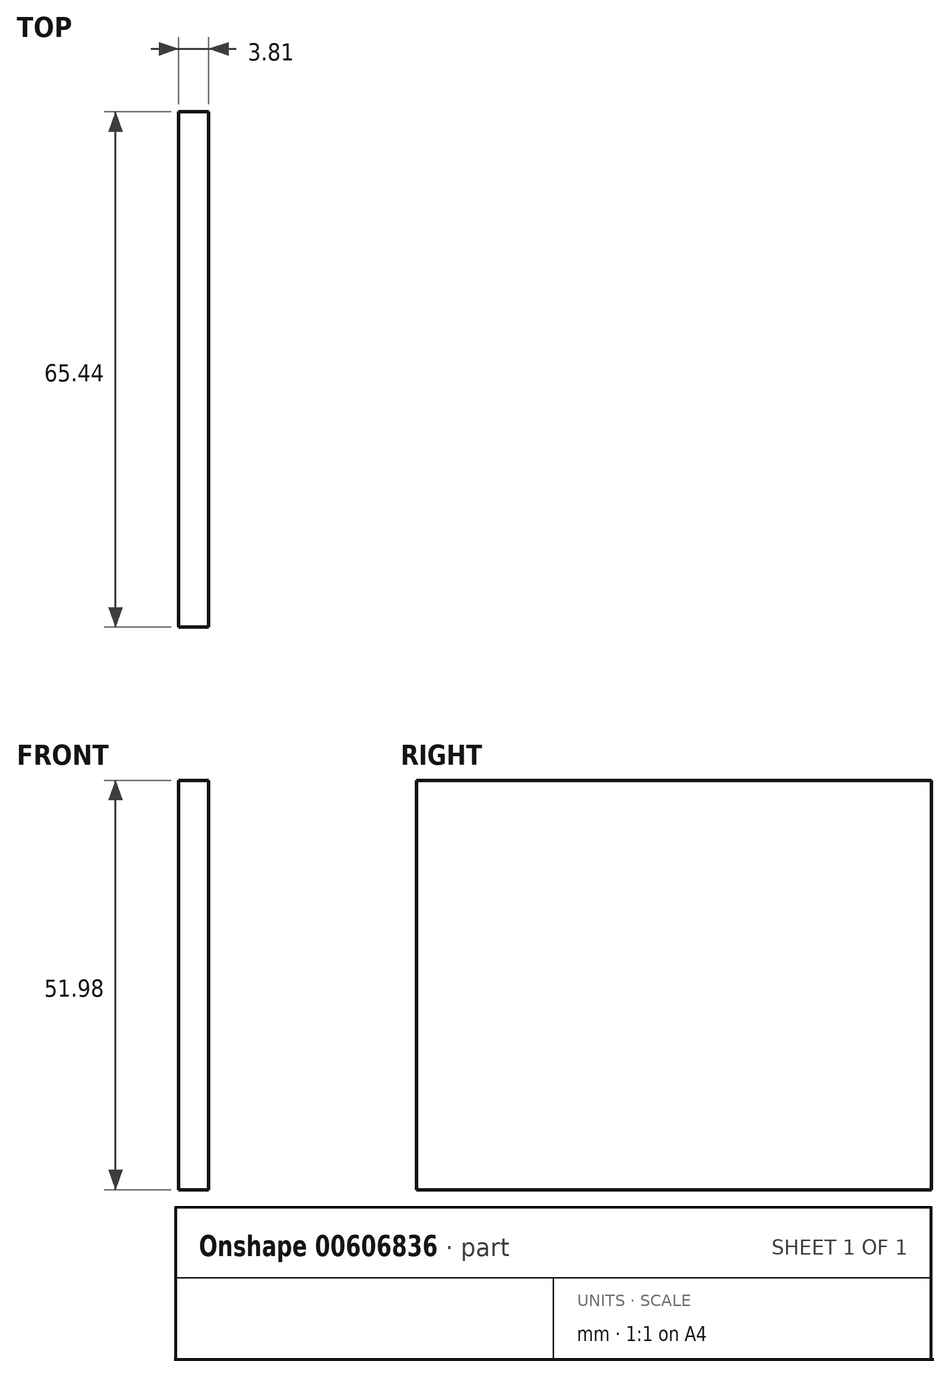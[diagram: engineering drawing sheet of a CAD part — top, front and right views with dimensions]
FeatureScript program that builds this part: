
annotation { "Feature Type Name" : "Feature", "Feature Type Description" : "" }
export const myFeature = defineFeature(function(context is Context, id is Id, definition is map)
    precondition{}
    {
        {
            var Q0;
            Q0=qCreatedBy(makeId("Right.planeOp"),FACE);
            var sketch = newSketch(context, id + "F0", { "sketchPlane" : qUnion([Q0])});
            skLineSegment(sketch, "E0.bottom", {"start": v(-65.44, 51.98) * mm, "end": v(0, 51.98) * mm});
            skLineSegment(sketch, "E0.top", {"start": v(-65.44, 0) * mm, "end": v(0, 0) * mm});
            skLineSegment(sketch, "E0.left", {"start": v(-65.44, 51.98) * mm, "end": v(-65.44, 0) * mm});
            skLineSegment(sketch, "E0.right", {"start": v(0, 51.98) * mm, "end": v(0, 0) * mm});
            skSolve(sketch);
        }
        {
            var Q0;
            Q0 = qSketchRegion(id + "F0", true);
            extrude(context, id + "F1", {"entities" : qUnion([Q0]), "depth" : 3.8 * mm, "offsetDistance" : 25.4 * mm});
        }
    });
